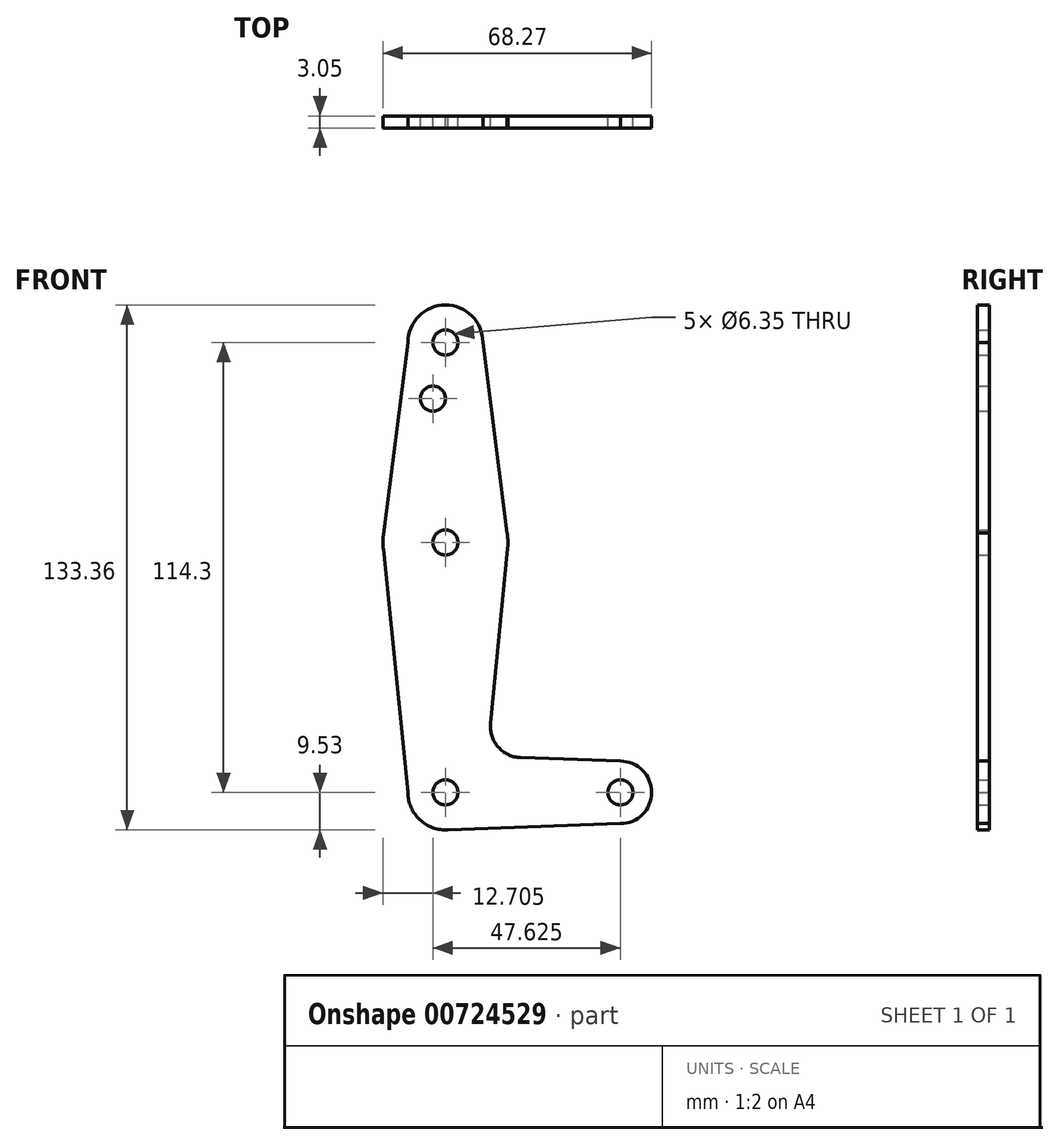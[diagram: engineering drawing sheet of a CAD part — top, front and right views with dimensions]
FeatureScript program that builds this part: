
annotation { "Feature Type Name" : "Feature", "Feature Type Description" : "" }
export const myFeature = defineFeature(function(context is Context, id is Id, definition is map)
    precondition{}
    {
        {
            var Q0;
            Q0=qCreatedBy(makeId("Front.planeOp"),FACE);
            var sketch = newSketch(context, id + "F0", { "sketchPlane" : qUnion([Q0])});
            skLineSegment(sketch, "E0", {"start": v(0, 0) * mm, "end": v(0, 114.3) * mm, "construction": true});
            skLineSegment(sketch, "E1", {"start": v(0, 0) * mm, "end": v(44.45, 0) * mm, "construction": true});
            skCircle(sketch, "E2", {"center": v(0, 114.3) * mm, "radius": 9.53 * mm});
            skCircle(sketch, "E3", {"center": v(0, 63.5) * mm, "radius": 15.88 * mm});
            skCircle(sketch, "E4", {"center": v(0, 0) * mm, "radius": 9.53 * mm});
            skCircle(sketch, "E5", {"center": v(44.45, 0) * mm, "radius": 7.94 * mm});
            skLineSegment(sketch, "E6", {"start": v(11.47, 17.56) * mm, "end": v(15.8, 61.96) * mm});
            skLineSegment(sketch, "E7", {"start": v(-9.53, 0) * mm, "end": v(-15.8, 61.96) * mm});
            skLineSegment(sketch, "E8", {"start": v(-9.53, 114.3) * mm, "end": v(-15.8, 65.1) * mm});
            skLineSegment(sketch, "E9", {"start": v(9.53, 114.3) * mm, "end": v(15.8, 65.1) * mm});
            skLineSegment(sketch, "E10", {"start": v(19.1, 8.84) * mm, "end": v(44.45, 7.94) * mm});
            skLineSegment(sketch, "E11", {"start": v(0, -9.52) * mm, "end": v(44.45, -7.94) * mm});
            skArc(sketch, "E12.filletArc", {"start": v(11.47, 17.56) * mm, "mid": v(13.4, 11.55) * mm, "end": v(19.1, 8.84) * mm});
            skCircle(sketch, "E13", {"center": v(0, 114.3) * mm, "radius": 3.18 * mm});
            skCircle(sketch, "E14", {"center": v(0, 63.5) * mm, "radius": 3.18 * mm});
            skCircle(sketch, "E15", {"center": v(0, 0) * mm, "radius": 3.18 * mm});
            skCircle(sketch, "E16", {"center": v(44.45, 0) * mm, "radius": 3.18 * mm});
            skCircle(sketch, "E17", {"center": v(-3.17, 100.03) * mm, "radius": 3.18 * mm});
            skSolve(sketch);
        }
        {
            var Q0;
            Q0=qSketchRegion(id+"F0",true);
            extrude(context, id + "F1", {"entities" : qUnion([Q0]), "depth" : 3.05 * mm});
        }
    });
